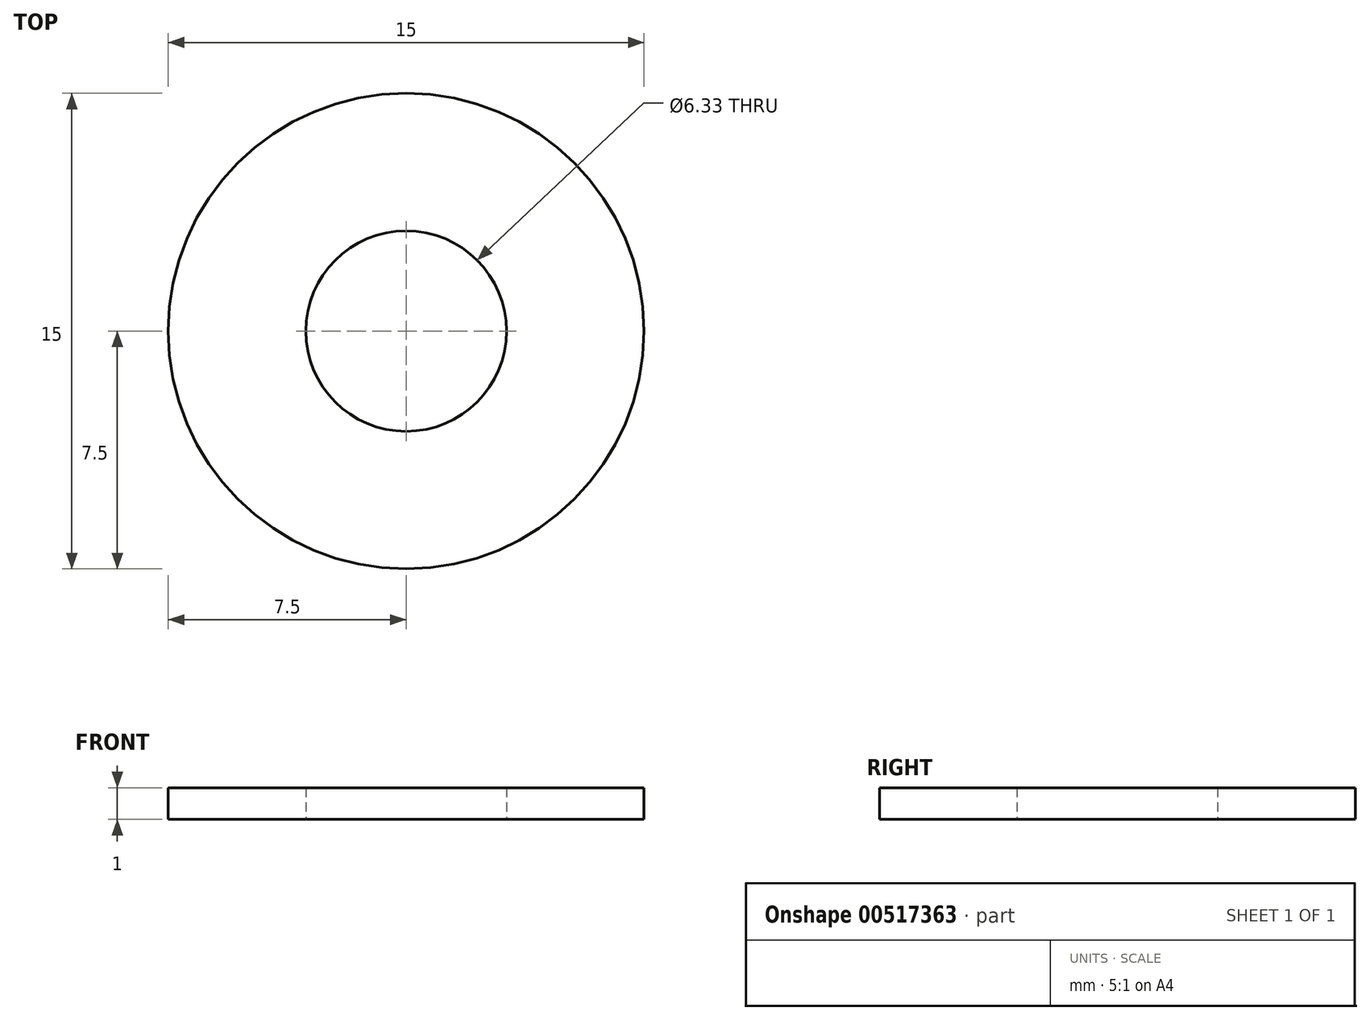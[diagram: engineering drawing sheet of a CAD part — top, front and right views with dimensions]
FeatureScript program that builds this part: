
annotation { "Feature Type Name" : "Feature", "Feature Type Description" : "" }
export const myFeature = defineFeature(function(context is Context, id is Id, definition is map)
    precondition{}
    {
        {
            var Q0;
            Q0=qCreatedBy(makeId("Top.planeOp"),FACE);
            var sketch = newSketch(context, id + "F0", { "sketchPlane" : qUnion([Q0])});
            skCircle(sketch, "E0", {"center": v(0, 0) * mm, "radius": 7.5 * mm});
            skCircle(sketch, "E1", {"center": v(0, 0) * mm, "radius": 3.16 * mm});
            skSolve(sketch);
        }
        {
            var Q0;
            Q0 = qSketchRegion(id + "F0", true);
            extrude(context, id + "F1", {"entities" : qUnion([Q0]), "depth" : 1 * mm, "offsetDistance" : 25 * mm});
        }
    });
